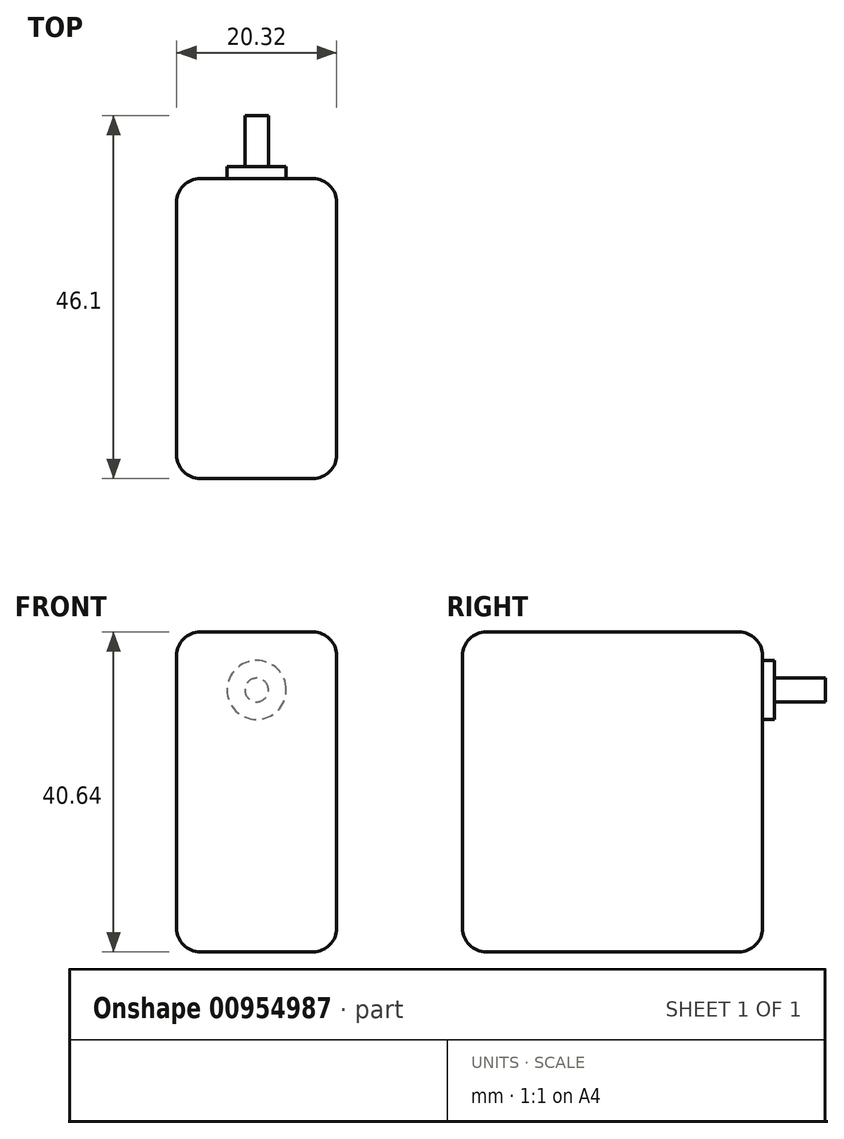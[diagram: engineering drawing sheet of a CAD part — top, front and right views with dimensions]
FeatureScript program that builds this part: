
annotation { "Feature Type Name" : "Feature", "Feature Type Description" : "" }
export const myFeature = defineFeature(function(context is Context, id is Id, definition is map)
    precondition{}
    {
        {
            var Q0;
            Q0=qCreatedBy(makeId("Front.planeOp"),FACE);
            var sketch = newSketch(context, id + "F0", { "sketchPlane" : qUnion([Q0])});
            skLineSegment(sketch, "E0.bottom", {"start": v(-10.16, 20.32) * mm, "end": v(10.16, 20.32) * mm});
            skLineSegment(sketch, "E0.top", {"start": v(-10.16, -20.32) * mm, "end": v(10.16, -20.32) * mm});
            skLineSegment(sketch, "E0.left", {"start": v(-10.16, 20.32) * mm, "end": v(-10.16, -20.32) * mm});
            skLineSegment(sketch, "E0.right", {"start": v(10.16, 20.32) * mm, "end": v(10.16, -20.32) * mm});
            skPoint(sketch, "E0.middle", {"position": v(0, 0) * mm});
            skCircle(sketch, "E1", {"center": v(0, 12.95) * mm, "radius": 3.75 * mm});
            skCircle(sketch, "E2", {"center": v(0, 12.95) * mm, "radius": 1.5 * mm});
            skSolve(sketch);
        }
        {
            var Q0;
            Q0 = qSketchRegion(id + "F0", true);
            var Q1;
            Q1=makeQuery(id+"F0.imprint","IMPRINT",FACE,{"disambiguationData":[TD([[makeQuery(id+"F0.imprint","IMPRINT",EDGE,{"derivedFrom":sQuery(id+"F0.wireOp",EDGE,"E1")}),1.0]])]});
            var Q2;
            Q2=makeQuery(id+"F0.imprint","IMPRINT",FACE,{"disambiguationData":[TD([[makeQuery(id+"F0.imprint","IMPRINT",EDGE,{"derivedFrom":sQuery(id+"F0.wireOp",EDGE,"E2")}),1.0]])]});
            extrude(context, id + "F1", {"entities" : qUnion([Q0, Q1, Q2]), "depth" : 38.1 * mm, "offsetDistance" : 25 * mm});
        }
        {
            var Q0;
            Q0=makeQuery(id+"F0.imprint","IMPRINT",FACE,{"disambiguationData":[TD([[makeQuery(id+"F0.imprint","IMPRINT",EDGE,{"derivedFrom":sQuery(id+"F0.wireOp",EDGE,"E1")}),1.0]])]});
            extrude(context, id + "F2", {"entities" : qUnion([Q0]), "operationType" : NewBodyOperationType.ADD, "oppositeDirection" : true, "depth" : 1.5 * mm, "offsetDistance" : 25 * mm});
        }
        {
            var Q0;
            Q0=makeQuery(id+"F1.opExtrude","SWEPT_FACE",FACE,{"disambiguationData":[OSD([sQuery(id+"F0.wireOp",EDGE,"E0.right")])]});
            var Q1;
            Q1=makeQuery(id+"F1.opExtrude","SWEPT_FACE",FACE,{"disambiguationData":[OSD([sQuery(id+"F0.wireOp",EDGE,"E0.bottom")])]});
            var Q2;
            Q2=makeQuery(id+"F1.opExtrude","SWEPT_FACE",FACE,{"disambiguationData":[OSD([sQuery(id+"F0.wireOp",EDGE,"E0.left")])]});
            var Q3;
            Q3=makeQuery(id+"F1.opExtrude","CAP_FACE",FACE,{"disambiguationData":[OSD([sQuery(id+"F0.wireOp",EDGE,"E0.bottom"),sQuery(id+"F0.wireOp",EDGE,"E0.top"),sQuery(id+"F0.wireOp",EDGE,"E0.left"),sQuery(id+"F0.wireOp",EDGE,"E0.right")])],"isStart":false});
            var Q4;
            Q4=makeQuery(id+"F1.opExtrude","SWEPT_FACE",FACE,{"disambiguationData":[OSD([sQuery(id+"F0.wireOp",EDGE,"E0.top")])]});
            fillet(context, id + "F3", {"entities" : qUnion([Q0, Q1, Q2, Q3, Q4]), "radius" : 3 * mm, "tangentPropagation" : true, "allowEdgeOverflow" : false});
        }
        {
            var Q0;
            Q0=makeQuery(id+"F0.imprint","IMPRINT",FACE,{"disambiguationData":[TD([[makeQuery(id+"F0.imprint","IMPRINT",EDGE,{"derivedFrom":sQuery(id+"F0.wireOp",EDGE,"E2")}),1.0]])]});
            extrude(context, id + "F4", {"entities" : qUnion([Q0]), "operationType" : NewBodyOperationType.ADD, "depth" : -8 * mm, "offsetDistance" : 25 * mm});
        }
    });
